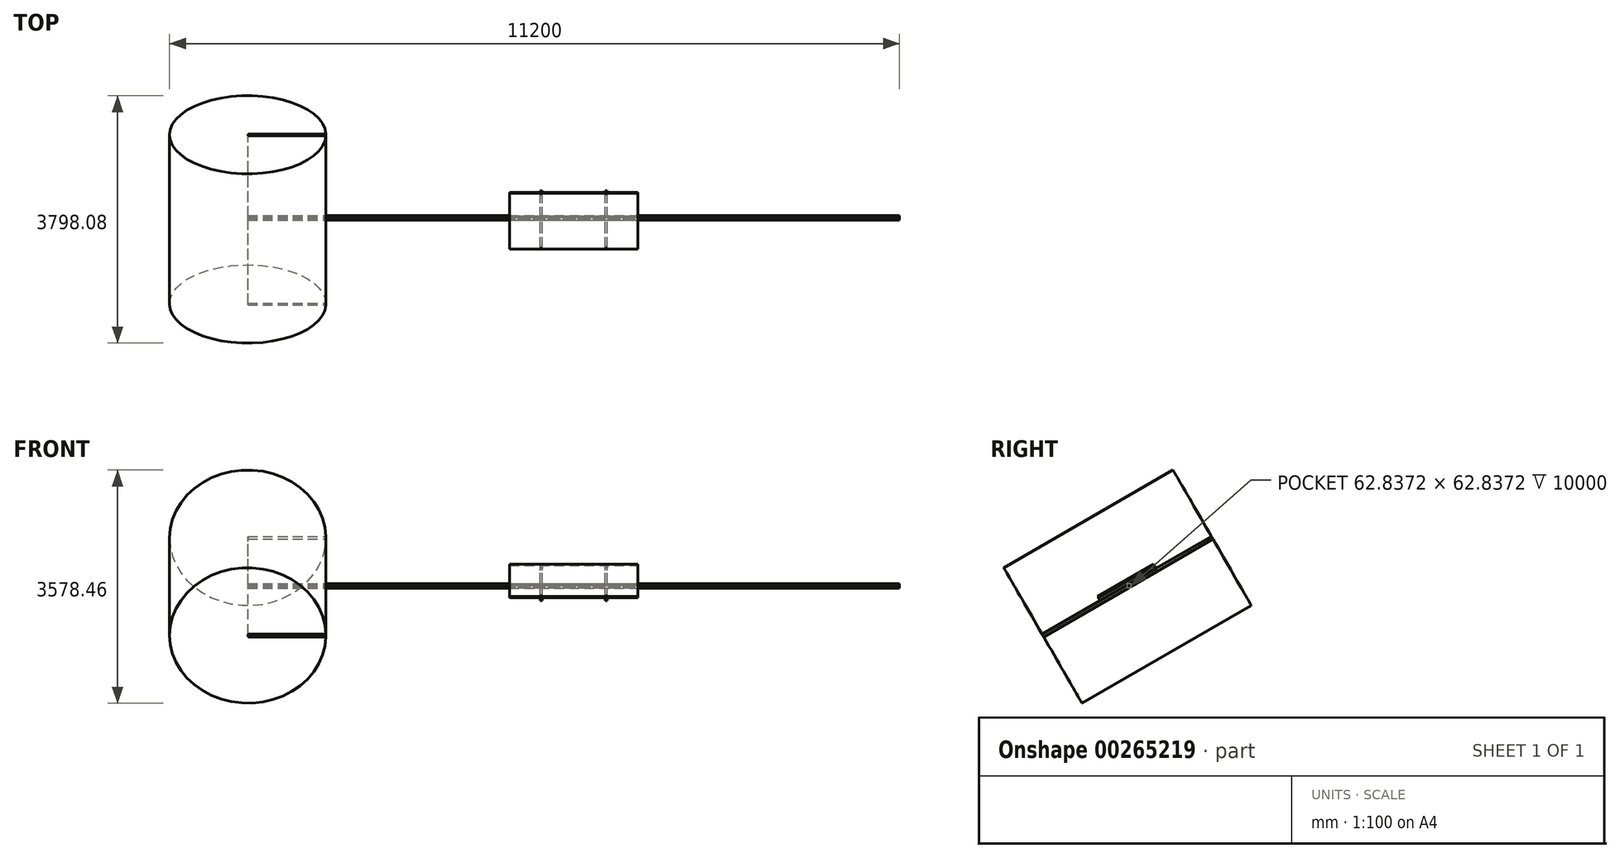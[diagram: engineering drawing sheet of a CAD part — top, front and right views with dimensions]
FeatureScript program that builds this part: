
annotation { "Feature Type Name" : "Feature", "Feature Type Description" : "" }
export const myFeature = defineFeature(function(context is Context, id is Id, definition is map)
    precondition{}
    {
        {
            var Q0;
            Q0=qCreatedBy(makeId("Top.planeOp"),FACE);
            var sketch = newSketch(context, id + "F0", { "sketchPlane" : qUnion([Q0])});
            skLineSegment(sketch, "E0.bottom", {"start": v(-568.11, 0.75) * mm, "end": v(1401.89, 0.75) * mm});
            skLineSegment(sketch, "E0.top", {"start": v(-568.11, 990.75) * mm, "end": v(1401.89, 990.75) * mm});
            skLineSegment(sketch, "E0.left", {"start": v(-568.11, 0.75) * mm, "end": v(-568.11, 990.75) * mm});
            skLineSegment(sketch, "E0.right", {"start": v(1401.89, 0.75) * mm, "end": v(1401.89, 990.75) * mm});
            skPoint(sketch, "E1.centerSnap0", {"position": v(416.89, 0.75) * mm});
            skPoint(sketch, "E1.centerSnap1", {"position": v(1401.89, 495.75) * mm});
            skCircle(sketch, "E2", {"center": v(916.89, 974.75) * mm, "radius": 6 * mm});
            skCircle(sketch, "E3", {"center": v(916.89, 16.75) * mm, "radius": 6 * mm});
            skCircle(sketch, "E4", {"center": v(-82.86, 16.84) * mm, "radius": 6 * mm});
            skCircle(sketch, "E5", {"center": v(-83.11, 974.75) * mm, "radius": 6 * mm});
            skSolve(sketch);
        }
        {
            var Q0;
            Q0 = qSketchRegion(id + "F0", true);
            extrude(context, id + "F1", {"entities" : qUnion([Q0]), "oppositeDirection" : true, "depth" : 25 * mm});
        }
        {
            var Q0;
            Q0=makeQuery(id+"F1.opExtrude","SWEPT_BODY",BODY,{"disambiguationData":[OSD([sQuery(id+"F0.wireOp",EDGE,"E0.bottom"),sQuery(id+"F0.wireOp",EDGE,"E0.top"),sQuery(id+"F0.wireOp",EDGE,"E0.left"),sQuery(id+"F0.wireOp",EDGE,"E0.right"),sQuery(id+"F0.wireOp",EDGE,"E2"),sQuery(id+"F0.wireOp",EDGE,"E3"),sQuery(id+"F0.wireOp",EDGE,"E4"),sQuery(id+"F0.wireOp",EDGE,"E5")])]});
            var Q1;
            Q1=makeQuery(id+"F1.opExtrude","CAP_EDGE",EDGE,{"disambiguationData":[OSD([sQuery(id+"F0.wireOp",EDGE,"E0.bottom")])],"isStart":false});
            transform(context, id + "F2", {"entities" : qUnion([Q0]), "transformType" : TransformType.ROTATION, "transformAxis" : qUnion([Q1]), "angle" : 30 * degree, "makeCopy" : false});
        }
        {
            var Q0;
            Q0=makeQuery(id+"F1.opExtrude","SWEPT_FACE",FACE,{"disambiguationData":[OSD([sQuery(id+"F0.wireOp",EDGE,"E0.top")])]});
            var sketch = newSketch(context, id + "F3", { "sketchPlane" : qUnion([Q0])});
            skLineSegment(sketch, "E6.bottom", {"start": v(98.11, -22.02) * mm, "end": v(68.11, -22.02) * mm});
            skLineSegment(sketch, "E6.top", {"start": v(98.11, -72.02) * mm, "end": v(68.11, -72.02) * mm});
            skLineSegment(sketch, "E6.left", {"start": v(98.11, -22.02) * mm, "end": v(98.11, -72.02) * mm});
            skLineSegment(sketch, "E6.right", {"start": v(68.11, -22.02) * mm, "end": v(68.11, -72.02) * mm});
            skLineSegment(sketch, "E7.MirrorCS", {"start": v(-901.89, -22.02) * mm, "end": v(-901.89, -72.02) * mm});
            skLineSegment(sketch, "E8.MirrorCS", {"start": v(-931.89, -72.02) * mm, "end": v(-901.89, -72.02) * mm});
            skLineSegment(sketch, "E9.MirrorCS", {"start": v(-931.89, -22.02) * mm, "end": v(-931.89, -72.02) * mm});
            skLineSegment(sketch, "E10.MirrorCS", {"start": v(-931.89, -22.02) * mm, "end": v(-901.89, -22.02) * mm});
            skSolve(sketch);
        }
        {
            var Q0;
            Q0 = qSketchRegion(id + "F3", true);
            extrude(context, id + "F4", {"entities" : qUnion([Q0]), "oppositeDirection" : true, "depth" : 990 * mm});
        }
        {
            var Q0;
            Q0=makeQuery(id+"F1.opExtrude","SWEPT_FACE",FACE,{"disambiguationData":[OSD([sQuery(id+"F0.wireOp",EDGE,"E0.left")])]});
            var sketch = newSketch(context, id + "F5", { "sketchPlane" : qUnion([Q0])});
            skLineSegment(sketch, "E11", {"start": v(-454.43, 179.2) * mm, "end": v(-432.78, 166.7) * mm});
            skLineSegment(sketch, "E12", {"start": v(-432.78, 166.7) * mm, "end": v(-457.78, 123.4) * mm});
            skLineSegment(sketch, "E13", {"start": v(-457.78, 123.4) * mm, "end": v(-501.08, 148.4) * mm});
            skLineSegment(sketch, "E14", {"start": v(-501.08, 148.4) * mm, "end": v(-476.08, 191.7) * mm});
            skLineSegment(sketch, "E15", {"start": v(-476.08, 191.7) * mm, "end": v(-454.43, 179.2) * mm});
            skSolve(sketch);
        }
        {
            var Q0;
            Q0=makeQuery(id+"F5.imprint","IMPRINT",FACE,{"disambiguationData":[TD([[makeQuery(id+"F5.imprint","IMPRINT",EDGE,{"derivedFrom":sQuery(id+"F5.wireOp",EDGE,"E11")}),-1.0]])]});
            extrude(context, id + "F6", {"entities" : qUnion([Q0]), "depth" : 4015 * mm, "hasSecondDirection" : true, "secondDirectionOppositeDirection" : true, "secondDirectionDepth" : 5985 * mm});
        }
        {
            var Q0;
            Q0=makeQuery(id+"F6.opExtrude","CAP_FACE",FACE,{"disambiguationData":[OSD([sQuery(id+"F5.wireOp",EDGE,"E11"),sQuery(id+"F5.wireOp",EDGE,"E12"),sQuery(id+"F5.wireOp",EDGE,"E13"),sQuery(id+"F5.wireOp",EDGE,"E14"),sQuery(id+"F5.wireOp",EDGE,"E15")])],"isStart":false});
            var Q1;
            Q1=makeQuery(id+"F6.opExtrude","CAP_FACE",FACE,{"disambiguationData":[OSD([sQuery(id+"F5.wireOp",EDGE,"E11"),sQuery(id+"F5.wireOp",EDGE,"E12"),sQuery(id+"F5.wireOp",EDGE,"E13"),sQuery(id+"F5.wireOp",EDGE,"E14"),sQuery(id+"F5.wireOp",EDGE,"E15")])],"isStart":true});
            var Q2;
            Q2=makeQuery(id+"F6.opExtrude","SWEPT_BODY",BODY,{"disambiguationData":[OSD([sQuery(id+"F5.wireOp",EDGE,"E11"),sQuery(id+"F5.wireOp",EDGE,"E12"),sQuery(id+"F5.wireOp",EDGE,"E13"),sQuery(id+"F5.wireOp",EDGE,"E14"),sQuery(id+"F5.wireOp",EDGE,"E15")])]});
            shell(context, id + "F7", {"entities" : qUnion([Q0, Q1]), "parts" : qUnion([Q2]), "thickness" : 2 * mm});
        }
        {
            var Q0;
            Q0=makeQuery(id+"F6.opExtrude","SWEPT_FACE",FACE,{"disambiguationData":[OSD([sQuery(id+"F5.wireOp",EDGE,"E12")])]});
            var sketch = newSketch(context, id + "F8", { "sketchPlane" : qUnion([Q0])});
            skCircle(sketch, "E16", {"center": v(-4583.11, -97.02) * mm, "radius": 1200 * mm});
            skSolve(sketch);
        }
        {
            var Q0;
            {var subQ1=sQuery(id+"F5.wireOp",EDGE,"E12");var subQ6=makeQuery(id+"F6.opExtrude","CAP_EDGE",EDGE,{"disambiguationData":[OSD([subQ1])],"isStart":false});Q0=makeQuery(id+"F8.imprint","IMPRINT",FACE,{"disambiguationData":[TD([[makeQuery(id+"F8.imprint","IMPRINT",EDGE,{"derivedFrom":subQ6}),-1.0]])]});}
            extrude(context, id + "F9", {"entities" : qUnion([Q0]), "operationType" : NewBodyOperationType.ADD, "endBound" : BoundingType.SYMMETRIC, "depth" : 3000 * mm});
        }
    });
